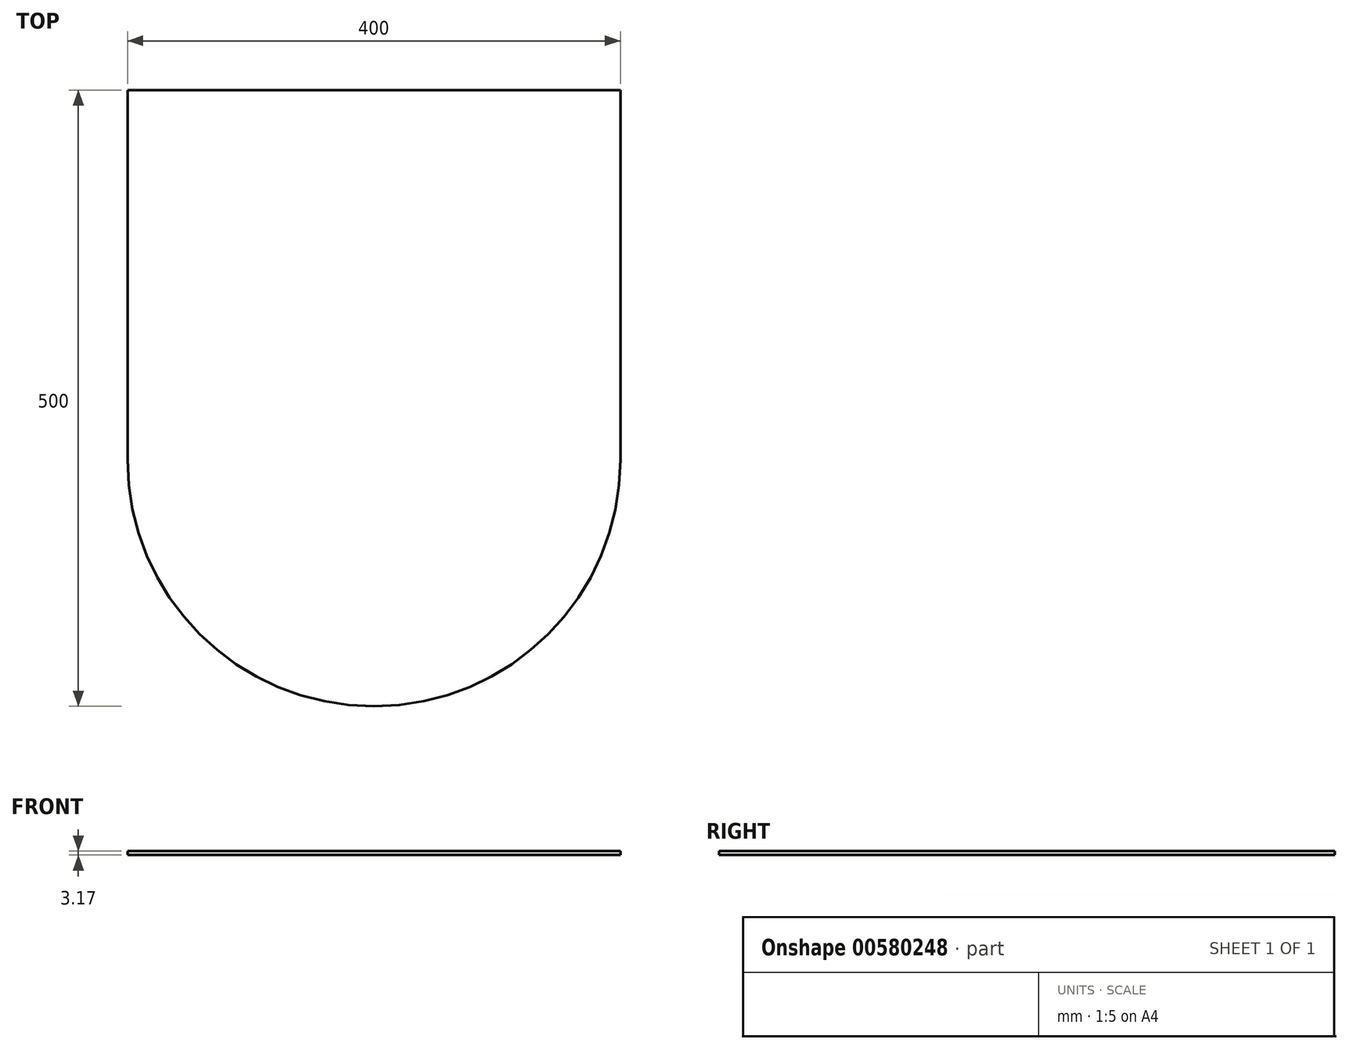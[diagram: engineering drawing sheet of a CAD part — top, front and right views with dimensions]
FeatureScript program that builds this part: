
annotation { "Feature Type Name" : "Feature", "Feature Type Description" : "" }
export const myFeature = defineFeature(function(context is Context, id is Id, definition is map)
    precondition{}
    {
        {
            var Q0;
            Q0=qCreatedBy(makeId("Top.planeOp"),FACE);
            var sketch = newSketch(context, id + "F0", { "sketchPlane" : qUnion([Q0])});
            skLineSegment(sketch, "E0", {"start": v(0, 0) * mm, "end": v(0, 300) * mm});
            skLineSegment(sketch, "E1", {"start": v(0, 300) * mm, "end": v(-200, 300) * mm});
            skLineSegment(sketch, "E2", {"start": v(0, 300) * mm, "end": v(200, 300) * mm});
            skLineSegment(sketch, "E3", {"start": v(-200, 300) * mm, "end": v(-200, 0) * mm});
            skLineSegment(sketch, "E4", {"start": v(-200, 0) * mm, "end": v(0, 0) * mm});
            skCircle(sketch, "E5", {"center": v(0, 0) * mm, "radius": 200 * mm});
            skLineSegment(sketch, "E6", {"start": v(200, 300) * mm, "end": v(200, 0) * mm});
            skSolve(sketch);
        }
        {
            var Q0;
            {var subQ0=sQuery(id+"F0.wireOp",EDGE,"E1");Q0=makeQuery(id+"F0.imprint","IMPRINT",FACE,{"disambiguationData":[TD([[makeQuery(id+"F0.imprint","IMPRINT",EDGE,{"derivedFrom":subQ0}),1.0]])]});}
            var Q1;
            {var subQ0=sQuery(id+"F0.wireOp",EDGE,"E2");Q1=makeQuery(id+"F0.imprint","IMPRINT",FACE,{"disambiguationData":[TD([[makeQuery(id+"F0.imprint","IMPRINT",EDGE,{"derivedFrom":subQ0}),-1.0]])]});}
            var Q2;
            {var subQ0=sQuery(id+"F0.wireOp",EDGE,"E4");Q2=makeQuery(id+"F0.imprint","IMPRINT",FACE,{"disambiguationData":[TD([[makeQuery(id+"F0.imprint","IMPRINT",EDGE,{"derivedFrom":subQ0}),1.0]])]});}
            var Q3;
            {var subQ0=sQuery(id+"F0.wireOp",EDGE,"E4");Q3=makeQuery(id+"F0.imprint","IMPRINT",FACE,{"disambiguationData":[TD([[makeQuery(id+"F0.imprint","IMPRINT",EDGE,{"derivedFrom":subQ0}),-1.0]])]});}
            extrude(context, id + "F1", {"entities" : qUnion([Q0, Q1, Q2, Q3]), "depth" : 3.17 * mm});
        }
    });
